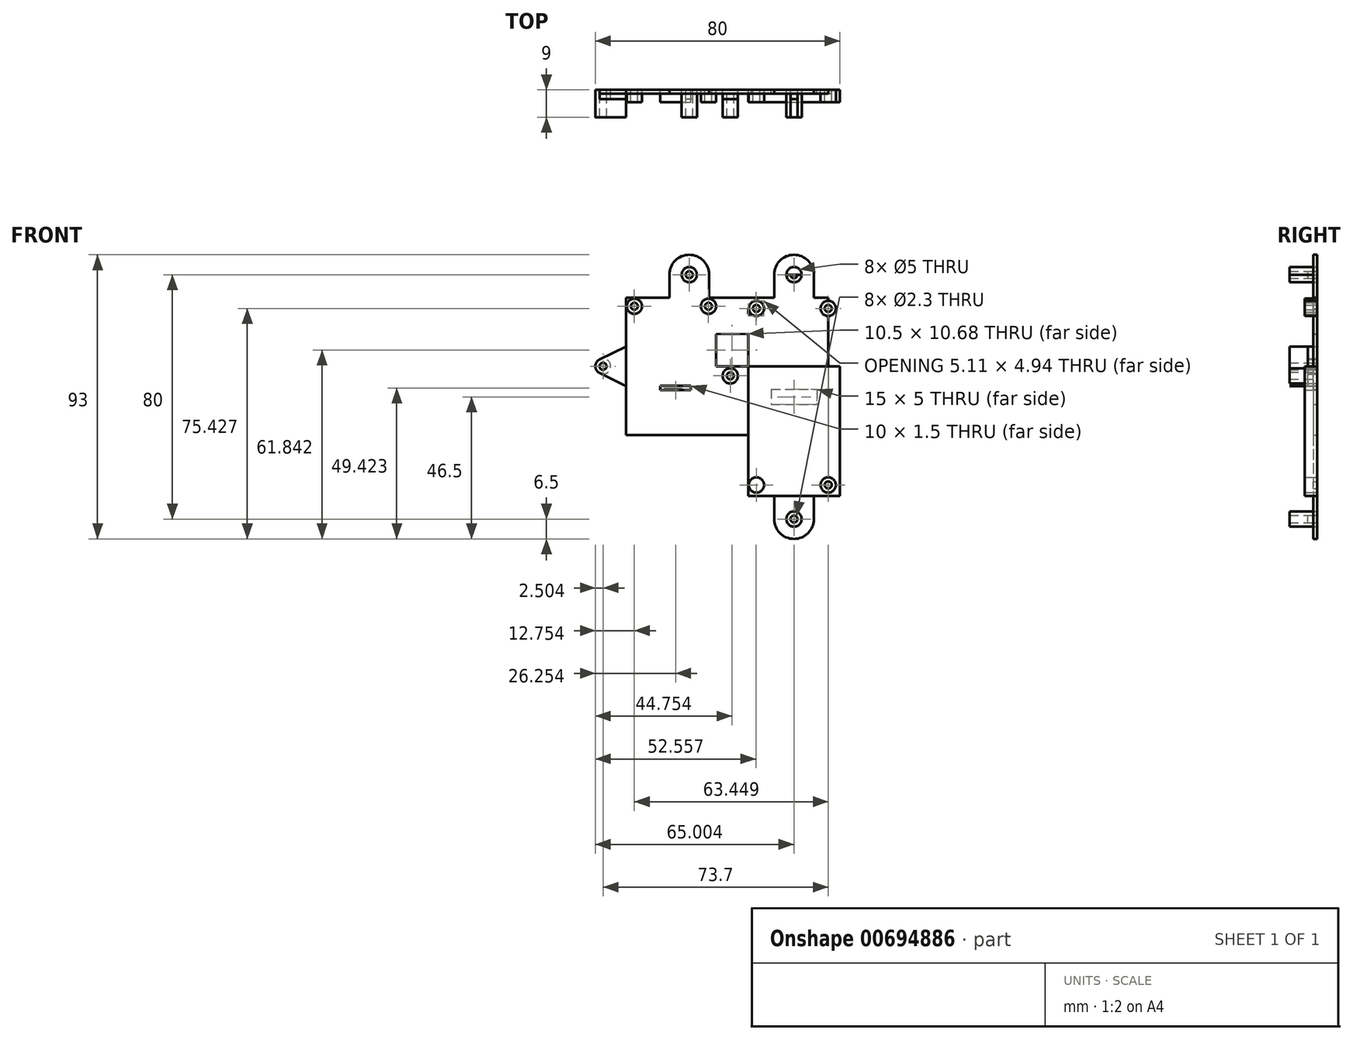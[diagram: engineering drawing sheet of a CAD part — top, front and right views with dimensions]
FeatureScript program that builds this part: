
annotation { "Feature Type Name" : "Feature", "Feature Type Description" : "" }
export const myFeature = defineFeature(function(context is Context, id is Id, definition is map)
    precondition{}
    {
        {
            var Q0;
            Q0=qCreatedBy(makeId("Front.planeOp"),FACE);
            var sketch = newSketch(context, id + "F0", { "sketchPlane" : qUnion([Q0])});
            skLineSegment(sketch, "E0.bottom", {"start": v(-16.83, 32.5) * mm, "end": v(13.17, 32.5) * mm});
            skLineSegment(sketch, "E0.top", {"start": v(-16.83, -32.5) * mm, "end": v(13.17, -32.5) * mm});
            skLineSegment(sketch, "E0.left", {"start": v(-16.83, 32.5) * mm, "end": v(-16.83, -32.5) * mm});
            skLineSegment(sketch, "E0.right", {"start": v(13.17, 32.5) * mm, "end": v(13.17, -32.5) * mm});
            skPoint(sketch, "E0.middle", {"position": v(-1.83, 0) * mm});
            skLineSegment(sketch, "E1.bottom", {"start": v(-16.83, 32.5) * mm, "end": v(-56.83, 32.5) * mm});
            skLineSegment(sketch, "E1.top", {"start": v(-16.83, -12.5) * mm, "end": v(-56.83, -12.5) * mm});
            skLineSegment(sketch, "E1.left", {"start": v(-16.83, 32.5) * mm, "end": v(-16.83, -12.5) * mm});
            skLineSegment(sketch, "E1.right", {"start": v(-56.83, 32.5) * mm, "end": v(-56.83, -12.5) * mm});
            skCircle(sketch, "E2", {"center": v(-54.08, 29.67) * mm, "radius": 2.5 * mm});
            skPoint(sketch, "E2.centerSnap0", {"position": v(-55.33, 29.67) * mm});
            skPoint(sketch, "E2.centerSnap1", {"position": v(-54.08, 30.92) * mm});
            skLineSegment(sketch, "E3", {"start": v(-51.33, 29.67) * mm, "end": v(-29.83, 29.67) * mm});
            skCircle(sketch, "E4", {"center": v(-29.83, 29.67) * mm, "radius": 2.5 * mm});
            skLineSegment(sketch, "E5", {"start": v(-40.58, 29.67) * mm, "end": v(-40.58, 3.67) * mm});
            skLineSegment(sketch, "E6", {"start": v(-40.58, 3.67) * mm, "end": v(-35.58, 3.67) * mm});
            skLineSegment(sketch, "E7", {"start": v(-35.58, 3.67) * mm, "end": v(-45.58, 3.67) * mm});
            skLineSegment(sketch, "E8", {"start": v(-45.58, 3.67) * mm, "end": v(-45.58, 2.17) * mm});
            skLineSegment(sketch, "E9", {"start": v(-45.58, 2.17) * mm, "end": v(-35.58, 2.17) * mm});
            skLineSegment(sketch, "E10", {"start": v(-35.58, 2.17) * mm, "end": v(-35.58, 3.67) * mm});
            skCircle(sketch, "E11", {"center": v(9.37, 28.95) * mm, "radius": 2.5 * mm});
            skPoint(sketch, "E11.centerSnap0", {"position": v(9.37, 30.2) * mm});
            skPoint(sketch, "E11.centerSnap1", {"position": v(10.87, 28.95) * mm});
            skLineSegment(sketch, "E12", {"start": v(-1.83, 0) * mm, "end": v(-1.83, 32.5) * mm});
            skLineSegment(sketch, "E13", {"start": v(9.37, 28.95) * mm, "end": v(-14.13, 28.95) * mm});
            skCircle(sketch, "E14", {"center": v(-14.13, 28.95) * mm, "radius": 2.5 * mm});
            skCircle(sketch, "E15.MirrorC", {"center": v(-14.13, -28.85) * mm, "radius": 2.5 * mm});
            skCircle(sketch, "E16.MirrorC", {"center": v(9.37, -28.85) * mm, "radius": 2.5 * mm});
            skLineSegment(sketch, "E17.bottom", {"start": v(-9.33, 2.5) * mm, "end": v(5.67, 2.5) * mm});
            skLineSegment(sketch, "E17.top", {"start": v(-9.33, -2.5) * mm, "end": v(5.67, -2.5) * mm});
            skLineSegment(sketch, "E17.left", {"start": v(-9.33, 2.5) * mm, "end": v(-9.33, -2.5) * mm});
            skLineSegment(sketch, "E17.right", {"start": v(5.67, 2.5) * mm, "end": v(5.67, -2.5) * mm});
            skCircle(sketch, "E18", {"center": v(9.37, 28.95) * mm, "radius": 1.15 * mm});
            skCircle(sketch, "E19", {"center": v(-14.13, 28.95) * mm, "radius": 1.15 * mm});
            skLineSegment(sketch, "E20", {"start": v(9.37, 28.95) * mm, "end": v(9.37, -26.35) * mm});
            skCircle(sketch, "E21", {"center": v(9.37, -28.85) * mm, "radius": 1.15 * mm});
            skCircle(sketch, "E22", {"center": v(-14.13, -28.85) * mm, "radius": 1.15 * mm});
            skCircle(sketch, "E23", {"center": v(-29.83, 29.67) * mm, "radius": 1.15 * mm});
            skCircle(sketch, "E24", {"center": v(-54.08, 29.67) * mm, "radius": 1.15 * mm});
            skLineSegment(sketch, "E25", {"start": v(-15.63, 27.12) * mm, "end": v(-24.08, 27.12) * mm});
            skCircle(sketch, "E26", {"center": v(-22.69, 6.88) * mm, "radius": 1.15 * mm});
            skCircle(sketch, "E27", {"center": v(-22.69, 6.88) * mm, "radius": 2.5 * mm});
            skLineSegment(sketch, "E28", {"start": v(9.37, -28.85) * mm, "end": v(9.37, -32.5) * mm});
            skLineSegment(sketch, "E29", {"start": v(9.37, -32.5) * mm, "end": v(13.17, -32.5) * mm});
            skLineSegment(sketch, "E30", {"start": v(-14.13, -28.85) * mm, "end": v(-14.13, -32.5) * mm});
            skLineSegment(sketch, "E31", {"start": v(-14.13, -32.5) * mm, "end": v(-16.83, -32.5) * mm});
            skLineSegment(sketch, "E32", {"start": v(9.37, 28.95) * mm, "end": v(9.37, 32.5) * mm});
            skLineSegment(sketch, "E33", {"start": v(9.37, 32.5) * mm, "end": v(13.17, 32.5) * mm});
            skLineSegment(sketch, "E34", {"start": v(-14.13, 28.95) * mm, "end": v(-16.83, 28.95) * mm});
            skLineSegment(sketch, "E35", {"start": v(-14.13, 28.95) * mm, "end": v(-14.13, 32.5) * mm});
            skLineSegment(sketch, "E36", {"start": v(-56.83, 10) * mm, "end": v(-64.33, 10) * mm});
            skCircle(sketch, "E37", {"center": v(-64.33, 10) * mm, "radius": 1.15 * mm});
            skCircle(sketch, "E38", {"center": v(-64.33, 10) * mm, "radius": 2.5 * mm});
            skLineSegment(sketch, "E39", {"start": v(-36.1, 32.5) * mm, "end": v(-36.1, 40) * mm});
            skCircle(sketch, "E40", {"center": v(-36.1, 40) * mm, "radius": 6.5 * mm});
            skCircle(sketch, "E41", {"center": v(-36.1, 40) * mm, "radius": 2.5 * mm});
            skCircle(sketch, "E42", {"center": v(-36.1, 40) * mm, "radius": 1.15 * mm});
            skLineSegment(sketch, "E43", {"start": v(-1.83, 32.5) * mm, "end": v(-1.83, 40) * mm});
            skCircle(sketch, "E44", {"center": v(-1.83, 40) * mm, "radius": 6.5 * mm});
            skCircle(sketch, "E45", {"center": v(-1.83, 40) * mm, "radius": 2.5 * mm});
            skCircle(sketch, "E46", {"center": v(-1.83, 40) * mm, "radius": 1.15 * mm});
            skCircle(sketch, "E47", {"center": v(-1.83, -40) * mm, "radius": 6.5 * mm});
            skCircle(sketch, "E48", {"center": v(-1.83, -40) * mm, "radius": 2.5 * mm});
            skCircle(sketch, "E49", {"center": v(-1.83, -40) * mm, "radius": 1.15 * mm});
            skLineSegment(sketch, "E50", {"start": v(-1.83, -40) * mm, "end": v(-1.83, -32.5) * mm});
            skLineSegment(sketch, "E51", {"start": v(-1.83, -40) * mm, "end": v(-8.33, -40) * mm});
            skLineSegment(sketch, "E52", {"start": v(-8.33, -40) * mm, "end": v(4.67, -40) * mm});
            skLineSegment(sketch, "E53", {"start": v(4.67, -40) * mm, "end": v(4.67, -32.5) * mm});
            skLineSegment(sketch, "E54", {"start": v(4.67, -32.5) * mm, "end": v(-8.33, -32.5) * mm});
            skLineSegment(sketch, "E55", {"start": v(-8.33, -32.5) * mm, "end": v(-8.33, -40) * mm});
            skLineSegment(sketch, "E56", {"start": v(-1.83, 40) * mm, "end": v(-8.33, 40) * mm});
            skLineSegment(sketch, "E57", {"start": v(-8.33, 40) * mm, "end": v(4.67, 40) * mm});
            skLineSegment(sketch, "E58", {"start": v(4.67, 40) * mm, "end": v(4.67, 32.5) * mm});
            skLineSegment(sketch, "E59", {"start": v(4.67, 32.5) * mm, "end": v(-8.33, 32.5) * mm});
            skLineSegment(sketch, "E60", {"start": v(-8.33, 32.5) * mm, "end": v(-8.33, 40) * mm});
            skLineSegment(sketch, "E61", {"start": v(-36.1, 40) * mm, "end": v(-42.6, 40) * mm});
            skLineSegment(sketch, "E62", {"start": v(-42.6, 40) * mm, "end": v(-42.6, 32.5) * mm});
            skLineSegment(sketch, "E63", {"start": v(-36.1, 40) * mm, "end": v(-29.6, 40) * mm});
            skLineSegment(sketch, "E64", {"start": v(-29.6, 40) * mm, "end": v(-29.6, 32.5) * mm});
            skLineSegment(sketch, "E65", {"start": v(-28.7, 20.53) * mm, "end": v(-16.83, 20.68) * mm});
            skLineSegment(sketch, "E66", {"start": v(-51.58, 29.67) * mm, "end": v(-32.33, 29.67) * mm});
            skLineSegment(sketch, "E67", {"start": v(-54.08, 29.67) * mm, "end": v(-56.83, 29.67) * mm});
            skLineSegment(sketch, "E68", {"start": v(-29.83, 29.67) * mm, "end": v(-27.33, 29.67) * mm});
            skLineSegment(sketch, "E69", {"start": v(-27.33, 29.67) * mm, "end": v(-27.33, 5.14) * mm});
            skLineSegment(sketch, "E70", {"start": v(-64.33, 10) * mm, "end": v(13.17, 10) * mm});
            skLineSegment(sketch, "E71", {"start": v(-56.83, 16.5) * mm, "end": v(-65.44, 12.24) * mm});
            skLineSegment(sketch, "E72", {"start": v(-56.83, 3.5) * mm, "end": v(-65.44, 7.76) * mm});
            skSolve(sketch);
        }
        {
            var Q0;
            Q0=makeQuery(id+"F0.imprint","IMPRINT",FACE,{"disambiguationData":[TD([[makeQuery(id+"F0.imprint","IMPRINT",EDGE,{"derivedFrom":sQuery(id+"F0.wireOp",EDGE,"E24")}),-1.0]])]});
            var Q1;
            Q1=makeQuery(id+"F0.imprint","IMPRINT",FACE,{"disambiguationData":[TD([[makeQuery(id+"F0.imprint","IMPRINT",EDGE,{"derivedFrom":sQuery(id+"F0.wireOp",EDGE,"E4")}),1.0]])]});
            var Q2;
            Q2=makeQuery(id+"F0.imprint","IMPRINT",FACE,{"disambiguationData":[TD([[makeQuery(id+"F0.imprint","IMPRINT",EDGE,{"derivedFrom":sQuery(id+"F0.wireOp",EDGE,"E19")}),-1.0]])]});
            var Q3;
            Q3=makeQuery(id+"F0.imprint","IMPRINT",FACE,{"disambiguationData":[TD([[makeQuery(id+"F0.imprint","IMPRINT",EDGE,{"derivedFrom":sQuery(id+"F0.wireOp",EDGE,"E18")}),-1.0]])]});
            var Q4;
            Q4=makeQuery(id+"F0.imprint","IMPRINT",FACE,{"disambiguationData":[TD([[makeQuery(id+"F0.imprint","IMPRINT",EDGE,{"derivedFrom":sQuery(id+"F0.wireOp",EDGE,"E15.MirrorC")}),-1.0]])]});
            var Q5;
            Q5=makeQuery(id+"F0.imprint","IMPRINT",FACE,{"disambiguationData":[TD([[makeQuery(id+"F0.imprint","IMPRINT",EDGE,{"derivedFrom":sQuery(id+"F0.wireOp",EDGE,"E16.MirrorC")}),-1.0]])]});
            var Q6;
            {var subQ0=sQuery(id+"F0.wireOp",EDGE,"E8");Q6=makeQuery(id+"F0.imprint","IMPRINT",FACE,{"disambiguationData":[TD([[makeQuery(id+"F0.imprint","IMPRINT",EDGE,{"derivedFrom":subQ0}),1.0]])]});}
            var Q7;
            {var subQ0=sQuery(id+"F0.wireOp",EDGE,"E17.top");Q7=makeQuery(id+"F0.imprint","IMPRINT",FACE,{"disambiguationData":[TD([[makeQuery(id+"F0.imprint","IMPRINT",EDGE,{"derivedFrom":subQ0}),1.0]])]});}
            var Q8;
            {var subQ5=sQuery(id+"F0.wireOp",EDGE,"E11");var subQ6=makeQuery(id+"F0.imprint","INTERSECT",VERTEX,{"derivedFrom":[subQ5,sQuery(id+"F0.wireOp",EDGE,"E20")]});Q8=makeQuery(id+"F0.imprint","IMPRINT",FACE,{"disambiguationData":[TD([[makeQuery(id+"F0.imprint","IMPRINT",EDGE,{"disambiguationData":[TD([[subQ6,1.0]])],"derivedFrom":subQ5}),1.0]])]});}
            var Q9;
            {var subQ1=sQuery(id+"F0.wireOp",EDGE,"E13");var subQ5=sQuery(id+"F0.wireOp",EDGE,"E14");var subQ8=makeQuery(id+"F0.imprint","INTERSECT",VERTEX,{"derivedFrom":[subQ1,subQ5]});Q9=makeQuery(id+"F0.imprint","IMPRINT",FACE,{"disambiguationData":[TD([[makeQuery(id+"F0.imprint","IMPRINT",EDGE,{"disambiguationData":[TD([[subQ8,-1.0]])],"derivedFrom":subQ1}),1.0]])]});}
            extrude(context, id + "F1", {"entities" : qUnion([Q0, Q1, Q2, Q3, Q4, Q5, Q6, Q7, Q8, Q9]), "depth" : 4 * mm, "offsetDistance" : 25 * mm});
        }
        {
            var Q0;
            {var subQ1=sQuery(id+"F0.wireOp",EDGE,"E11");var subQ13=sQuery(id+"F0.wireOp",EDGE,"E20");var subQ15=makeQuery(id+"F0.imprint","INTERSECT",VERTEX,{"derivedFrom":[subQ1,subQ13]});Q0=makeQuery(id+"F0.imprint","IMPRINT",FACE,{"disambiguationData":[TD([[makeQuery(id+"F0.imprint","IMPRINT",EDGE,{"disambiguationData":[TD([[subQ15,1.0]])],"derivedFrom":subQ1}),-1.0]])]});}
            var Q1;
            {var subQ1=sQuery(id+"F0.wireOp",EDGE,"E1.left");var subQ16=makeQuery(id+"F0.imprint","IMPRINT",VERTEX,{"disambiguationData":[OD(0.0)],"derivedFrom":subQ1});Q1=makeQuery(id+"F0.imprint","IMPRINT",FACE,{"disambiguationData":[TD([[makeQuery(id+"F0.imprint","IMPRINT",EDGE,{"disambiguationData":[TD([[subQ16,-1.0]])],"derivedFrom":subQ1}),1.0]])]});}
            var Q2;
            {var subQ0=sQuery(id+"F0.wireOp",EDGE,"E12");var subQ5=sQuery(id+"F0.wireOp",EDGE,"E13");var subQ6=makeQuery(id+"F0.imprint","INTERSECT",VERTEX,{"derivedFrom":[subQ0,subQ5]});Q2=makeQuery(id+"F0.imprint","IMPRINT",FACE,{"disambiguationData":[TD([[makeQuery(id+"F0.imprint","IMPRINT",EDGE,{"disambiguationData":[TD([[subQ6,1.0]])],"derivedFrom":subQ5}),-1.0]])]});}
            var Q3;
            {var subQ0=sQuery(id+"F0.wireOp",EDGE,"E12");var subQ5=sQuery(id+"F0.wireOp",EDGE,"E13");var subQ6=makeQuery(id+"F0.imprint","INTERSECT",VERTEX,{"derivedFrom":[subQ0,subQ5]});Q3=makeQuery(id+"F0.imprint","IMPRINT",FACE,{"disambiguationData":[TD([[makeQuery(id+"F0.imprint","IMPRINT",EDGE,{"disambiguationData":[TD([[subQ6,-1.0]])],"derivedFrom":subQ5}),-1.0]])]});}
            var Q4;
            {var subQ0=sQuery(id+"F0.wireOp",EDGE,"E35");var subQ1=sQuery(id+"F0.wireOp",EDGE,"E0.bottom");var subQ2=makeQuery(id+"F0.imprint","INTERSECT",VERTEX,{"derivedFrom":[subQ1,subQ0]});Q4=makeQuery(id+"F0.imprint","IMPRINT",FACE,{"disambiguationData":[TD([[makeQuery(id+"F0.imprint","IMPRINT",EDGE,{"disambiguationData":[TD([[subQ2,-1.0]])],"derivedFrom":subQ1}),-1.0]])]});}
            var Q5;
            {var subQ9=sQuery(id+"F0.wireOp",EDGE,"E33");Q5=makeQuery(id+"F0.imprint","IMPRINT",FACE,{"disambiguationData":[TD([[makeQuery(id+"F0.imprint","IMPRINT",EDGE,{"derivedFrom":subQ9}),-1.0]])]});}
            var Q6;
            {var subQ3=sQuery(id+"F0.wireOp",EDGE,"E11");var subQ7=sQuery(id+"F0.wireOp",EDGE,"E13");var subQ9=makeQuery(id+"F0.imprint","INTERSECT",VERTEX,{"derivedFrom":[subQ3,subQ7]});Q6=makeQuery(id+"F0.imprint","IMPRINT",FACE,{"disambiguationData":[TD([[makeQuery(id+"F0.imprint","IMPRINT",EDGE,{"disambiguationData":[TD([[subQ9,1.0]])],"derivedFrom":subQ3}),-1.0]])]});}
            var Q7;
            {var subQ0=sQuery(id+"F0.wireOp",EDGE,"E44");var subQ1=sQuery(id+"F0.wireOp",EDGE,"E12");var subQ2=makeQuery(id+"F0.imprint","INTERSECT",VERTEX,{"derivedFrom":[subQ1,subQ0]});Q7=makeQuery(id+"F0.imprint","IMPRINT",FACE,{"disambiguationData":[TD([[makeQuery(id+"F0.imprint","IMPRINT",EDGE,{"disambiguationData":[TD([[subQ2,-1.0]])],"derivedFrom":subQ1}),-1.0]])]});}
            var Q8;
            {var subQ0=sQuery(id+"F0.wireOp",EDGE,"E45");Q8=makeQuery(id+"F0.imprint","IMPRINT",FACE,{"disambiguationData":[TD([[makeQuery(id+"F0.imprint","IMPRINT",EDGE,{"derivedFrom":subQ0}),-1.0]])]});}
            var Q9;
            {var subQ0=sQuery(id+"F0.wireOp",EDGE,"E44");var subQ1=sQuery(id+"F0.wireOp",EDGE,"E12");var subQ2=makeQuery(id+"F0.imprint","INTERSECT",VERTEX,{"derivedFrom":[subQ1,subQ0]});Q9=makeQuery(id+"F0.imprint","IMPRINT",FACE,{"disambiguationData":[TD([[makeQuery(id+"F0.imprint","IMPRINT",EDGE,{"disambiguationData":[TD([[subQ2,-1.0]])],"derivedFrom":subQ1}),1.0]])]});}
            var Q10;
            Q10=makeQuery(id+"F0.imprint","IMPRINT",FACE,{"disambiguationData":[TD([[makeQuery(id+"F0.imprint","IMPRINT",EDGE,{"derivedFrom":sQuery(id+"F0.wireOp",EDGE,"E15.MirrorC")}),1.0]])]});
            var Q11;
            {var subQ7=sQuery(id+"F0.wireOp",EDGE,"E29");Q11=makeQuery(id+"F0.imprint","IMPRINT",FACE,{"disambiguationData":[TD([[makeQuery(id+"F0.imprint","IMPRINT",EDGE,{"derivedFrom":subQ7}),1.0]])]});}
            var Q12;
            {var subQ0=sQuery(id+"F0.wireOp",EDGE,"E47");var subQ1=sQuery(id+"F0.wireOp",EDGE,"E0.top");var subQ2=makeQuery(id+"F0.imprint","INTERSECT",VERTEX,{"disambiguationData":[OD(0.0)],"derivedFrom":[subQ1,subQ0]});Q12=makeQuery(id+"F0.imprint","IMPRINT",FACE,{"disambiguationData":[TD([[makeQuery(id+"F0.imprint","IMPRINT",EDGE,{"disambiguationData":[TD([[subQ2,-1.0]])],"derivedFrom":subQ1}),1.0]])]});}
            var Q13;
            {var subQ3=sQuery(id+"F0.wireOp",EDGE,"E48");Q13=makeQuery(id+"F0.imprint","IMPRINT",FACE,{"disambiguationData":[TD([[makeQuery(id+"F0.imprint","IMPRINT",EDGE,{"derivedFrom":subQ3}),-1.0]])]});}
            var Q14;
            {var subQ1=sQuery(id+"F0.wireOp",EDGE,"E1.top");var subQ4=sQuery(id+"F0.wireOp",EDGE,"H2bswWBa-21Oe-qWVp-0FWu-aY4BrK7KTLVz");var subQ5=makeQuery(id+"F0.imprint","INTERSECT",VERTEX,{"derivedFrom":[subQ1,subQ4]});Q14=makeQuery(id+"F0.imprint","IMPRINT",FACE,{"disambiguationData":[TD([[makeQuery(id+"F0.imprint","IMPRINT",EDGE,{"disambiguationData":[TD([[subQ5,1.0]])],"derivedFrom":subQ1}),-1.0]])]});}
            var Q15;
            {var subQ1=sQuery(id+"F0.wireOp",EDGE,"E0.left");var subQ4=sQuery(id+"F0.wireOp",EDGE,"H2bswWBa-21Oe-qWVp-0FWu-aY4BrK7KTLVz");var subQ5=makeQuery(id+"F0.imprint","INTERSECT",VERTEX,{"derivedFrom":[subQ1,subQ4]});Q15=makeQuery(id+"F0.imprint","IMPRINT",FACE,{"disambiguationData":[TD([[makeQuery(id+"F0.imprint","IMPRINT",EDGE,{"disambiguationData":[TD([[subQ5,1.0]])],"derivedFrom":subQ1}),1.0]])]});}
            var Q16;
            {var subQ0=sQuery(id+"F0.wireOp",EDGE,"H2bswWBa-21Oe-qWVp-0FWu-aY4BrK7KTLVz");var subQ1=sQuery(id+"F0.wireOp",EDGE,"E0.left");var subQ2=makeQuery(id+"F0.imprint","INTERSECT",VERTEX,{"derivedFrom":[subQ1,subQ0]});Q16=makeQuery(id+"F0.imprint","IMPRINT",FACE,{"disambiguationData":[TD([[makeQuery(id+"F0.imprint","IMPRINT",EDGE,{"disambiguationData":[TD([[subQ2,1.0]])],"derivedFrom":subQ1}),-1.0]])]});}
            var Q17;
            Q17=makeQuery(id+"F0.imprint","IMPRINT",FACE,{"disambiguationData":[TD([[makeQuery(id+"F0.imprint","IMPRINT",EDGE,{"derivedFrom":sQuery(id+"F0.wireOp",EDGE,"E2")}),-1.0]])]});
            var Q18;
            {var subQ0=sQuery(id+"F0.wireOp",EDGE,"E5");var subQ1=sQuery(id+"F0.wireOp",EDGE,"E3");var subQ2=makeQuery(id+"F0.imprint","INTERSECT",VERTEX,{"derivedFrom":[subQ1,subQ0]});Q18=makeQuery(id+"F0.imprint","IMPRINT",FACE,{"disambiguationData":[TD([[makeQuery(id+"F0.imprint","IMPRINT",EDGE,{"disambiguationData":[TD([[subQ2,1.0]])],"derivedFrom":subQ1}),-1.0]])]});}
            var Q19;
            {var subQ0=sQuery(id+"F0.wireOp",EDGE,"E5");var subQ1=sQuery(id+"F0.wireOp",EDGE,"E3");var subQ2=makeQuery(id+"F0.imprint","INTERSECT",VERTEX,{"derivedFrom":[subQ1,subQ0]});Q19=makeQuery(id+"F0.imprint","IMPRINT",FACE,{"disambiguationData":[TD([[makeQuery(id+"F0.imprint","IMPRINT",EDGE,{"disambiguationData":[TD([[subQ2,-1.0]])],"derivedFrom":subQ1}),-1.0]])]});}
            var Q20;
            {var subQ5=sQuery(id+"F0.wireOp",EDGE,"E1.bottom");var subQ6=makeQuery(id+"F0.imprint","INTERSECT",VERTEX,{"derivedFrom":[subQ5,sQuery(id+"F0.wireOp",EDGE,"E41")]});Q20=makeQuery(id+"F0.imprint","IMPRINT",FACE,{"disambiguationData":[TD([[makeQuery(id+"F0.imprint","IMPRINT",EDGE,{"disambiguationData":[TD([[subQ6,1.0]])],"derivedFrom":subQ5}),1.0]])]});}
            var Q21;
            {var subQ0=sQuery(id+"F0.wireOp",EDGE,"E41");Q21=makeQuery(id+"F0.imprint","IMPRINT",FACE,{"disambiguationData":[TD([[makeQuery(id+"F0.imprint","IMPRINT",EDGE,{"derivedFrom":subQ0}),-1.0]])]});}
            var Q22;
            {var subQ0=sQuery(id+"F0.wireOp",EDGE,"E1.right");var subQ1=makeQuery(id+"F0.imprint","INTERSECT",VERTEX,{"derivedFrom":[subQ0,sQuery(id+"F0.wireOp",EDGE,"E38")]});Q22=makeQuery(id+"F0.imprint","IMPRINT",FACE,{"disambiguationData":[TD([[makeQuery(id+"F0.imprint","IMPRINT",EDGE,{"disambiguationData":[TD([[subQ1,1.0]])],"derivedFrom":subQ0}),1.0]])]});}
            var Q23;
            {var subQ0=sQuery(id+"F0.wireOp",EDGE,"E38");Q23=makeQuery(id+"F0.imprint","IMPRINT",FACE,{"disambiguationData":[TD([[makeQuery(id+"F0.imprint","IMPRINT",EDGE,{"derivedFrom":subQ0}),-1.0]])]});}
            var Q24;
            {var subQ0=sQuery(id+"F0.wireOp",EDGE,"E32");var subQ1=sQuery(id+"F0.wireOp",EDGE,"E13");var subQ2=makeQuery(id+"F0.imprint","INTERSECT",VERTEX,{"derivedFrom":[subQ1,subQ0]});Q24=makeQuery(id+"F0.imprint","IMPRINT",FACE,{"disambiguationData":[TD([[makeQuery(id+"F0.imprint","IMPRINT",EDGE,{"disambiguationData":[TD([[subQ2,-1.0]])],"derivedFrom":subQ1}),1.0]])]});}
            var Q25;
            {var subQ0=sQuery(id+"F0.wireOp",EDGE,"E32");var subQ1=sQuery(id+"F0.wireOp",EDGE,"E13");var subQ2=makeQuery(id+"F0.imprint","INTERSECT",VERTEX,{"derivedFrom":[subQ1,subQ0]});Q25=makeQuery(id+"F0.imprint","IMPRINT",FACE,{"disambiguationData":[TD([[makeQuery(id+"F0.imprint","IMPRINT",EDGE,{"disambiguationData":[TD([[subQ2,-1.0]])],"derivedFrom":subQ1}),-1.0]])]});}
            var Q26;
            {var subQ1=sQuery(id+"F0.wireOp",EDGE,"E13");var subQ3=sQuery(id+"F0.wireOp",EDGE,"E19");var subQ4=makeQuery(id+"F0.imprint","INTERSECT",VERTEX,{"derivedFrom":[subQ1,subQ3]});Q26=makeQuery(id+"F0.imprint","IMPRINT",FACE,{"disambiguationData":[TD([[makeQuery(id+"F0.imprint","IMPRINT",EDGE,{"disambiguationData":[TD([[subQ4,1.0]])],"derivedFrom":subQ3}),1.0]])]});}
            var Q27;
            {var subQ0=sQuery(id+"F0.wireOp",EDGE,"E35");var subQ1=sQuery(id+"F0.wireOp",EDGE,"E19");var subQ2=makeQuery(id+"F0.imprint","INTERSECT",VERTEX,{"derivedFrom":[subQ1,subQ0]});Q27=makeQuery(id+"F0.imprint","IMPRINT",FACE,{"disambiguationData":[TD([[makeQuery(id+"F0.imprint","IMPRINT",EDGE,{"disambiguationData":[TD([[subQ2,-1.0]])],"derivedFrom":subQ1}),1.0]])]});}
            var Q28;
            {var subQ1=sQuery(id+"F0.wireOp",EDGE,"E13");var subQ3=sQuery(id+"F0.wireOp",EDGE,"E19");var subQ4=makeQuery(id+"F0.imprint","INTERSECT",VERTEX,{"derivedFrom":[subQ1,subQ3]});Q28=makeQuery(id+"F0.imprint","IMPRINT",FACE,{"disambiguationData":[TD([[makeQuery(id+"F0.imprint","IMPRINT",EDGE,{"disambiguationData":[TD([[subQ4,-1.0]])],"derivedFrom":subQ3}),1.0]])]});}
            var Q29;
            Q29=makeQuery(id+"F0.imprint","IMPRINT",FACE,{"disambiguationData":[TD([[makeQuery(id+"F0.imprint","IMPRINT",EDGE,{"derivedFrom":sQuery(id+"F0.wireOp",EDGE,"E23")}),1.0]])]});
            var Q30;
            Q30=makeQuery(id+"F0.imprint","IMPRINT",FACE,{"disambiguationData":[TD([[makeQuery(id+"F0.imprint","IMPRINT",EDGE,{"derivedFrom":sQuery(id+"F0.wireOp",EDGE,"E24")}),1.0]])]});
            var Q31;
            Q31=makeQuery(id+"F0.imprint","IMPRINT",FACE,{"disambiguationData":[TD([[makeQuery(id+"F0.imprint","IMPRINT",EDGE,{"derivedFrom":sQuery(id+"F0.wireOp",EDGE,"E21")}),1.0]])]});
            var Q32;
            Q32=makeQuery(id+"F0.imprint","IMPRINT",FACE,{"disambiguationData":[TD([[makeQuery(id+"F0.imprint","IMPRINT",EDGE,{"derivedFrom":sQuery(id+"F0.wireOp",EDGE,"E22")}),1.0]])]});
            var Q33;
            {var subQ1=sQuery(id+"F0.wireOp",EDGE,"E0.left");var subQ3=sQuery(id+"F0.wireOp",EDGE,"vLtY0Nj5-JtJk-fO2F-L4fz-pWqKutG9Hdl8");var subQ4=makeQuery(id+"F0.imprint","INTERSECT",VERTEX,{"derivedFrom":[subQ1,subQ3]});Q33=makeQuery(id+"F0.imprint","IMPRINT",FACE,{"disambiguationData":[TD([[makeQuery(id+"F0.imprint","IMPRINT",EDGE,{"disambiguationData":[TD([[subQ4,-1.0]])],"derivedFrom":subQ3}),-1.0]])]});}
            var Q34;
            {var subQ3=sQuery(id+"F0.wireOp",EDGE,"s8Qitc2e-HOJI-ncwY-YY4z-nysmE6fKBLHD");Q34=makeQuery(id+"F0.imprint","IMPRINT",FACE,{"disambiguationData":[TD([[makeQuery(id+"F0.imprint","IMPRINT",EDGE,{"derivedFrom":subQ3}),1.0]])]});}
            var Q35;
            {var subQ3=sQuery(id+"F0.wireOp",EDGE,"rnlotXtN-yekX-c3Ef-nKGb-O9DUJwXdL25D");Q35=makeQuery(id+"F0.imprint","IMPRINT",FACE,{"disambiguationData":[TD([[makeQuery(id+"F0.imprint","IMPRINT",EDGE,{"derivedFrom":subQ3}),-1.0]])]});}
            var Q36;
            {var subQ3=sQuery(id+"F0.wireOp",EDGE,"E62");Q36=makeQuery(id+"F0.imprint","IMPRINT",FACE,{"disambiguationData":[TD([[makeQuery(id+"F0.imprint","IMPRINT",EDGE,{"derivedFrom":subQ3}),1.0]])]});}
            var Q37;
            {var subQ3=sQuery(id+"F0.wireOp",EDGE,"E64");Q37=makeQuery(id+"F0.imprint","IMPRINT",FACE,{"disambiguationData":[TD([[makeQuery(id+"F0.imprint","IMPRINT",EDGE,{"derivedFrom":subQ3}),-1.0]])]});}
            var Q38;
            {var subQ5=sQuery(id+"F0.wireOp",EDGE,"E60");Q38=makeQuery(id+"F0.imprint","IMPRINT",FACE,{"disambiguationData":[TD([[makeQuery(id+"F0.imprint","IMPRINT",EDGE,{"derivedFrom":subQ5}),-1.0]])]});}
            var Q39;
            {var subQ5=sQuery(id+"F0.wireOp",EDGE,"E58");Q39=makeQuery(id+"F0.imprint","IMPRINT",FACE,{"disambiguationData":[TD([[makeQuery(id+"F0.imprint","IMPRINT",EDGE,{"derivedFrom":subQ5}),-1.0]])]});}
            var Q40;
            {var subQ0=sQuery(id+"F0.wireOp",EDGE,"wpgFawej-uTnE-nY6H-FU0d-e7JS0PavbXeQ");var subQ1=sQuery(id+"F0.wireOp",EDGE,"9S27bfH2-aeVg-8c6K-cwQt-1v0k5dwx2PAc");var subQ2=makeQuery(id+"F0.imprint","INTERSECT",VERTEX,{"derivedFrom":[subQ1,subQ0]});Q40=makeQuery(id+"F0.imprint","IMPRINT",FACE,{"disambiguationData":[TD([[makeQuery(id+"F0.imprint","IMPRINT",EDGE,{"disambiguationData":[TD([[subQ2,-1.0]])],"derivedFrom":subQ1}),-1.0]])]});}
            var Q41;
            {var subQ0=sQuery(id+"F0.wireOp",EDGE,"wpgFawej-uTnE-nY6H-FU0d-e7JS0PavbXeQ");var subQ1=sQuery(id+"F0.wireOp",EDGE,"9S27bfH2-aeVg-8c6K-cwQt-1v0k5dwx2PAc");var subQ2=makeQuery(id+"F0.imprint","INTERSECT",VERTEX,{"derivedFrom":[subQ1,subQ0]});Q41=makeQuery(id+"F0.imprint","IMPRINT",FACE,{"disambiguationData":[TD([[makeQuery(id+"F0.imprint","IMPRINT",EDGE,{"disambiguationData":[TD([[subQ2,-1.0]])],"derivedFrom":subQ1}),1.0]])]});}
            var Q42;
            {var subQ0=sQuery(id+"F0.wireOp",EDGE,"WzKnqnnp-cW6H-dtaq-a9nc-BIZvJngSIy6v");var subQ5=sQuery(id+"F0.wireOp",EDGE,"wpgFawej-uTnE-nY6H-FU0d-e7JS0PavbXeQ");var subQ6=makeQuery(id+"F0.imprint","INTERSECT",VERTEX,{"derivedFrom":[subQ5,subQ0]});Q42=makeQuery(id+"F0.imprint","IMPRINT",FACE,{"disambiguationData":[TD([[makeQuery(id+"F0.imprint","IMPRINT",EDGE,{"disambiguationData":[TD([[subQ6,-1.0]])],"derivedFrom":subQ5}),-1.0]])]});}
            var Q43;
            {var subQ0=sQuery(id+"F0.wireOp",EDGE,"TDiUslce-FG7m-lDCQ-hQCu-48WjQpyJGrM8");var subQ1=sQuery(id+"F0.wireOp",EDGE,"Gpz7nxuA-fGOU-zDca-uDqp-oelFocvOXtPt");var subQ2=makeQuery(id+"F0.imprint","INTERSECT",VERTEX,{"derivedFrom":[subQ1,subQ0]});Q43=makeQuery(id+"F0.imprint","IMPRINT",FACE,{"disambiguationData":[TD([[makeQuery(id+"F0.imprint","IMPRINT",EDGE,{"disambiguationData":[TD([[subQ2,-1.0]])],"derivedFrom":subQ1}),-1.0]])]});}
            var Q44;
            {var subQ1=sQuery(id+"F0.wireOp",EDGE,"E1.top");var subQ3=sQuery(id+"F0.wireOp",EDGE,"9S27bfH2-aeVg-8c6K-cwQt-1v0k5dwx2PAc");var subQ4=makeQuery(id+"F0.imprint","INTERSECT",VERTEX,{"derivedFrom":[subQ1,subQ3]});Q44=makeQuery(id+"F0.imprint","IMPRINT",FACE,{"disambiguationData":[TD([[makeQuery(id+"F0.imprint","IMPRINT",EDGE,{"disambiguationData":[TD([[subQ4,1.0]])],"derivedFrom":subQ3}),-1.0]])]});}
            var Q45;
            {var subQ3=sQuery(id+"F0.wireOp",EDGE,"U70AJvk3-q6Ap-TPiJ-vSA6-dHJ4n5ZZM8l7");Q45=makeQuery(id+"F0.imprint","IMPRINT",FACE,{"disambiguationData":[TD([[makeQuery(id+"F0.imprint","IMPRINT",EDGE,{"derivedFrom":subQ3}),-1.0]])]});}
            var Q46;
            {var subQ0=sQuery(id+"F0.wireOp",EDGE,"TDiUslce-FG7m-lDCQ-hQCu-48WjQpyJGrM8");var subQ1=sQuery(id+"F0.wireOp",EDGE,"Gpz7nxuA-fGOU-zDca-uDqp-oelFocvOXtPt");var subQ2=makeQuery(id+"F0.imprint","INTERSECT",VERTEX,{"derivedFrom":[subQ1,subQ0]});Q46=makeQuery(id+"F0.imprint","IMPRINT",FACE,{"disambiguationData":[TD([[makeQuery(id+"F0.imprint","IMPRINT",EDGE,{"disambiguationData":[TD([[subQ2,-1.0]])],"derivedFrom":subQ1}),1.0]])]});}
            var Q47;
            {var subQ0=sQuery(id+"F0.wireOp",EDGE,"E55");Q47=makeQuery(id+"F0.imprint","IMPRINT",FACE,{"disambiguationData":[TD([[makeQuery(id+"F0.imprint","IMPRINT",EDGE,{"derivedFrom":subQ0}),1.0]])]});}
            var Q48;
            {var subQ0=sQuery(id+"F0.wireOp",EDGE,"E53");Q48=makeQuery(id+"F0.imprint","IMPRINT",FACE,{"disambiguationData":[TD([[makeQuery(id+"F0.imprint","IMPRINT",EDGE,{"derivedFrom":subQ0}),1.0]])]});}
            var Q49;
            {var subQ3=sQuery(id+"F0.wireOp",EDGE,"E14");var subQ5=sQuery(id+"F0.wireOp",EDGE,"E35");var subQ6=makeQuery(id+"F0.imprint","INTERSECT",VERTEX,{"derivedFrom":[subQ3,subQ5]});Q49=makeQuery(id+"F0.imprint","IMPRINT",FACE,{"disambiguationData":[TD([[makeQuery(id+"F0.imprint","IMPRINT",EDGE,{"disambiguationData":[TD([[subQ6,-1.0]])],"derivedFrom":subQ3}),-1.0]])]});}
            var Q50;
            {var subQ9=sQuery(id+"F0.wireOp",EDGE,"LjoRHYEq-4y9t-VGf0-s3ML-qFKd4Cbp655V");var subQ10=sQuery(id+"F0.wireOp",EDGE,"E1.left");var subQ11=makeQuery(id+"F0.imprint","INTERSECT",VERTEX,{"derivedFrom":[subQ10,subQ9]});Q50=makeQuery(id+"F0.imprint","IMPRINT",FACE,{"disambiguationData":[TD([[makeQuery(id+"F0.imprint","IMPRINT",EDGE,{"disambiguationData":[TD([[subQ11,1.0]])],"derivedFrom":subQ10}),1.0]])]});}
            var Q51;
            {var subQ0=sQuery(id+"F0.wireOp",EDGE,"E34");var subQ1=sQuery(id+"F0.wireOp",EDGE,"E1.left");var subQ2=makeQuery(id+"F0.imprint","INTERSECT",VERTEX,{"derivedFrom":[subQ1,subQ0]});Q51=makeQuery(id+"F0.imprint","IMPRINT",FACE,{"disambiguationData":[TD([[makeQuery(id+"F0.imprint","IMPRINT",EDGE,{"disambiguationData":[TD([[subQ2,-1.0]])],"derivedFrom":subQ1}),1.0]])]});}
            var Q52;
            {var subQ0=sQuery(id+"F0.wireOp",EDGE,"E32");var subQ1=sQuery(id+"F0.wireOp",EDGE,"E18");var subQ2=makeQuery(id+"F0.imprint","INTERSECT",VERTEX,{"derivedFrom":[subQ1,subQ0]});Q52=makeQuery(id+"F0.imprint","IMPRINT",FACE,{"disambiguationData":[TD([[makeQuery(id+"F0.imprint","IMPRINT",EDGE,{"disambiguationData":[TD([[subQ2,1.0]])],"derivedFrom":subQ1}),1.0]])]});}
            var Q53;
            {var subQ0=sQuery(id+"F0.wireOp",EDGE,"E66");var subQ3=sQuery(id+"F0.wireOp",EDGE,"E5");var subQ4=makeQuery(id+"F0.imprint","INTERSECT",VERTEX,{"derivedFrom":[subQ3,subQ0]});Q53=makeQuery(id+"F0.imprint","IMPRINT",FACE,{"disambiguationData":[TD([[makeQuery(id+"F0.imprint","IMPRINT",EDGE,{"disambiguationData":[TD([[subQ4,-1.0]])],"derivedFrom":subQ3}),1.0]])]});}
            var Q54;
            {var subQ0=sQuery(id+"F0.wireOp",EDGE,"E65");var subQ1=sQuery(id+"F0.wireOp",EDGE,"E1.left");var subQ2=makeQuery(id+"F0.imprint","INTERSECT",VERTEX,{"derivedFrom":[subQ1,subQ0]});Q54=makeQuery(id+"F0.imprint","IMPRINT",FACE,{"disambiguationData":[TD([[makeQuery(id+"F0.imprint","IMPRINT",EDGE,{"disambiguationData":[TD([[subQ2,-1.0]])],"derivedFrom":subQ1}),-1.0]])]});}
            extrude(context, id + "F2", {"entities" : qUnion([Q0, Q1, Q2, Q3, Q4, Q5, Q6, Q7, Q8, Q9, Q10, Q11, Q12, Q13, Q14, Q15, Q16, Q17, Q18, Q19, Q20, Q21, Q22, Q23, Q24, Q25, Q26, Q27, Q28, Q29, Q30, Q31, Q32, Q33, Q34, Q35, Q36, Q37, Q38, Q39, Q40, Q41, Q42, Q43, Q44, Q45, Q46, Q47, Q48, Q49, Q50, Q51, Q52, Q53, Q54]), "depth" : 1.2 * mm, "offsetDistance" : 25 * mm});
        }
        {
            var Q0;
            {var subQ0=sQuery(id+"F0.wireOp",EDGE,"z3bIMlkc-Sqp3-YFfb-OgYx-sXrnVvqoU3hI");var subQ1=sQuery(id+"F0.wireOp",EDGE,"E37");var subQ2=makeQuery(id+"F0.imprint","INTERSECT",VERTEX,{"disambiguationData":[OD(0.0)],"derivedFrom":[subQ1,subQ0]});Q0=makeQuery(id+"F0.imprint","IMPRINT",FACE,{"disambiguationData":[TD([[makeQuery(id+"F0.imprint","IMPRINT",EDGE,{"disambiguationData":[TD([[subQ2,-1.0]])],"derivedFrom":subQ1}),-1.0]])]});}
            var Q1;
            {var subQ0=sQuery(id+"F0.wireOp",EDGE,"E38");var subQ1=sQuery(id+"F0.wireOp",EDGE,"E36");var subQ2=makeQuery(id+"F0.imprint","INTERSECT",VERTEX,{"derivedFrom":[subQ1,subQ0]});Q1=makeQuery(id+"F0.imprint","IMPRINT",FACE,{"disambiguationData":[TD([[makeQuery(id+"F0.imprint","IMPRINT",EDGE,{"disambiguationData":[TD([[subQ2,-1.0]])],"derivedFrom":subQ1}),-1.0]])]});}
            var Q2;
            {var subQ0=sQuery(id+"F0.wireOp",EDGE,"E38");var subQ1=sQuery(id+"F0.wireOp",EDGE,"E36");var subQ2=makeQuery(id+"F0.imprint","INTERSECT",VERTEX,{"derivedFrom":[subQ1,subQ0]});Q2=makeQuery(id+"F0.imprint","IMPRINT",FACE,{"disambiguationData":[TD([[makeQuery(id+"F0.imprint","IMPRINT",EDGE,{"disambiguationData":[TD([[subQ2,-1.0]])],"derivedFrom":subQ1}),1.0]])]});}
            var Q3;
            Q3=makeQuery(id+"F0.imprint","IMPRINT",FACE,{"disambiguationData":[TD([[makeQuery(id+"F0.imprint","IMPRINT",EDGE,{"derivedFrom":sQuery(id+"F0.wireOp",EDGE,"E26")}),-1.0]])]});
            var Q4;
            {var subQ0=sQuery(id+"F0.wireOp",EDGE,"wpgFawej-uTnE-nY6H-FU0d-e7JS0PavbXeQ");var subQ1=sQuery(id+"F0.wireOp",EDGE,"Gpz7nxuA-fGOU-zDca-uDqp-oelFocvOXtPt");var subQ2=makeQuery(id+"F0.imprint","INTERSECT",VERTEX,{"derivedFrom":[subQ1,subQ0]});Q4=makeQuery(id+"F0.imprint","IMPRINT",FACE,{"disambiguationData":[TD([[makeQuery(id+"F0.imprint","IMPRINT",EDGE,{"disambiguationData":[TD([[subQ2,-1.0]])],"derivedFrom":subQ1}),-1.0]])]});}
            var Q5;
            {var subQ0=sQuery(id+"F0.wireOp",EDGE,"Suqf36BG-M7e0-ZgLu-wpgL-xeVtndynmz1x");var subQ1=sQuery(id+"F0.wireOp",EDGE,"9S27bfH2-aeVg-8c6K-cwQt-1v0k5dwx2PAc");var subQ2=makeQuery(id+"F0.imprint","INTERSECT",VERTEX,{"derivedFrom":[subQ1,subQ0]});Q5=makeQuery(id+"F0.imprint","IMPRINT",FACE,{"disambiguationData":[TD([[makeQuery(id+"F0.imprint","IMPRINT",EDGE,{"disambiguationData":[TD([[subQ2,-1.0]])],"derivedFrom":subQ1}),-1.0]])]});}
            var Q6;
            {var subQ0=sQuery(id+"F0.wireOp",EDGE,"Suqf36BG-M7e0-ZgLu-wpgL-xeVtndynmz1x");var subQ1=sQuery(id+"F0.wireOp",EDGE,"9S27bfH2-aeVg-8c6K-cwQt-1v0k5dwx2PAc");var subQ2=makeQuery(id+"F0.imprint","INTERSECT",VERTEX,{"derivedFrom":[subQ1,subQ0]});Q6=makeQuery(id+"F0.imprint","IMPRINT",FACE,{"disambiguationData":[TD([[makeQuery(id+"F0.imprint","IMPRINT",EDGE,{"disambiguationData":[TD([[subQ2,-1.0]])],"derivedFrom":subQ1}),1.0]])]});}
            var Q7;
            {var subQ0=sQuery(id+"F0.wireOp",EDGE,"WzKnqnnp-cW6H-dtaq-a9nc-BIZvJngSIy6v");var subQ1=sQuery(id+"F0.wireOp",EDGE,"wpgFawej-uTnE-nY6H-FU0d-e7JS0PavbXeQ");var subQ2=makeQuery(id+"F0.imprint","INTERSECT",VERTEX,{"derivedFrom":[subQ1,subQ0]});Q7=makeQuery(id+"F0.imprint","IMPRINT",FACE,{"disambiguationData":[TD([[makeQuery(id+"F0.imprint","IMPRINT",EDGE,{"disambiguationData":[TD([[subQ2,-1.0]])],"derivedFrom":subQ1}),1.0]])]});}
            var Q8;
            {var subQ0=sQuery(id+"F0.wireOp",EDGE,"wpgFawej-uTnE-nY6H-FU0d-e7JS0PavbXeQ");var subQ1=sQuery(id+"F0.wireOp",EDGE,"Gpz7nxuA-fGOU-zDca-uDqp-oelFocvOXtPt");var subQ2=makeQuery(id+"F0.imprint","INTERSECT",VERTEX,{"derivedFrom":[subQ1,subQ0]});Q8=makeQuery(id+"F0.imprint","IMPRINT",FACE,{"disambiguationData":[TD([[makeQuery(id+"F0.imprint","IMPRINT",EDGE,{"disambiguationData":[TD([[subQ2,-1.0]])],"derivedFrom":subQ1}),1.0]])]});}
            var Q9;
            {var subQ0=sQuery(id+"F0.wireOp",EDGE,"E61");var subQ1=sQuery(id+"F0.wireOp",EDGE,"E41");var subQ2=makeQuery(id+"F0.imprint","INTERSECT",VERTEX,{"derivedFrom":[subQ1,subQ0]});Q9=makeQuery(id+"F0.imprint","IMPRINT",FACE,{"disambiguationData":[TD([[makeQuery(id+"F0.imprint","IMPRINT",EDGE,{"disambiguationData":[TD([[subQ2,1.0]])],"derivedFrom":subQ1}),1.0]])]});}
            var Q10;
            {var subQ0=sQuery(id+"F0.wireOp",EDGE,"E41");var subQ1=sQuery(id+"F0.wireOp",EDGE,"E39");var subQ2=makeQuery(id+"F0.imprint","INTERSECT",VERTEX,{"derivedFrom":[subQ1,subQ0]});Q10=makeQuery(id+"F0.imprint","IMPRINT",FACE,{"disambiguationData":[TD([[makeQuery(id+"F0.imprint","IMPRINT",EDGE,{"disambiguationData":[TD([[subQ2,-1.0]])],"derivedFrom":subQ1}),-1.0]])]});}
            var Q11;
            {var subQ0=sQuery(id+"F0.wireOp",EDGE,"E41");var subQ1=sQuery(id+"F0.wireOp",EDGE,"E39");var subQ2=makeQuery(id+"F0.imprint","INTERSECT",VERTEX,{"derivedFrom":[subQ1,subQ0]});Q11=makeQuery(id+"F0.imprint","IMPRINT",FACE,{"disambiguationData":[TD([[makeQuery(id+"F0.imprint","IMPRINT",EDGE,{"disambiguationData":[TD([[subQ2,-1.0]])],"derivedFrom":subQ1}),1.0]])]});}
            var Q12;
            {var subQ0=sQuery(id+"F0.wireOp",EDGE,"E57");var subQ1=sQuery(id+"F0.wireOp",EDGE,"E45");var subQ2=makeQuery(id+"F0.imprint","INTERSECT",VERTEX,{"disambiguationData":[OD(0.0)],"derivedFrom":[subQ1,subQ0]});Q12=makeQuery(id+"F0.imprint","IMPRINT",FACE,{"disambiguationData":[TD([[makeQuery(id+"F0.imprint","IMPRINT",EDGE,{"disambiguationData":[TD([[subQ2,1.0]])],"derivedFrom":subQ1}),1.0]])]});}
            var Q13;
            {var subQ0=sQuery(id+"F0.wireOp",EDGE,"E45");var subQ1=sQuery(id+"F0.wireOp",EDGE,"E43");var subQ2=makeQuery(id+"F0.imprint","INTERSECT",VERTEX,{"derivedFrom":[subQ1,subQ0]});Q13=makeQuery(id+"F0.imprint","IMPRINT",FACE,{"disambiguationData":[TD([[makeQuery(id+"F0.imprint","IMPRINT",EDGE,{"disambiguationData":[TD([[subQ2,-1.0]])],"derivedFrom":subQ1}),1.0]])]});}
            var Q14;
            {var subQ0=sQuery(id+"F0.wireOp",EDGE,"E45");var subQ1=sQuery(id+"F0.wireOp",EDGE,"E43");var subQ2=makeQuery(id+"F0.imprint","INTERSECT",VERTEX,{"derivedFrom":[subQ1,subQ0]});Q14=makeQuery(id+"F0.imprint","IMPRINT",FACE,{"disambiguationData":[TD([[makeQuery(id+"F0.imprint","IMPRINT",EDGE,{"disambiguationData":[TD([[subQ2,-1.0]])],"derivedFrom":subQ1}),-1.0]])]});}
            var Q15;
            {var subQ0=sQuery(id+"F0.wireOp",EDGE,"E50");var subQ1=sQuery(id+"F0.wireOp",EDGE,"E48");var subQ2=makeQuery(id+"F0.imprint","INTERSECT",VERTEX,{"derivedFrom":[subQ1,subQ0]});Q15=makeQuery(id+"F0.imprint","IMPRINT",FACE,{"disambiguationData":[TD([[makeQuery(id+"F0.imprint","IMPRINT",EDGE,{"disambiguationData":[TD([[subQ2,1.0]])],"derivedFrom":subQ1}),1.0]])]});}
            var Q16;
            {var subQ0=sQuery(id+"F0.wireOp",EDGE,"E50");var subQ1=sQuery(id+"F0.wireOp",EDGE,"E48");var subQ2=makeQuery(id+"F0.imprint","INTERSECT",VERTEX,{"derivedFrom":[subQ1,subQ0]});Q16=makeQuery(id+"F0.imprint","IMPRINT",FACE,{"disambiguationData":[TD([[makeQuery(id+"F0.imprint","IMPRINT",EDGE,{"disambiguationData":[TD([[subQ2,-1.0]])],"derivedFrom":subQ1}),1.0]])]});}
            var Q17;
            {var subQ0=sQuery(id+"F0.wireOp",EDGE,"E52");var subQ1=sQuery(id+"F0.wireOp",EDGE,"E48");var subQ2=makeQuery(id+"F0.imprint","INTERSECT",VERTEX,{"disambiguationData":[OD(0.0)],"derivedFrom":[subQ1,subQ0]});Q17=makeQuery(id+"F0.imprint","IMPRINT",FACE,{"disambiguationData":[TD([[makeQuery(id+"F0.imprint","IMPRINT",EDGE,{"disambiguationData":[TD([[subQ2,1.0]])],"derivedFrom":subQ1}),1.0]])]});}
            var Q18;
            {var subQ0=sQuery(id+"F0.wireOp",EDGE,"z3bIMlkc-Sqp3-YFfb-OgYx-sXrnVvqoU3hI");var subQ1=sQuery(id+"F0.wireOp",EDGE,"E37");var subQ2=makeQuery(id+"F0.imprint","INTERSECT",VERTEX,{"disambiguationData":[OD(0.0)],"derivedFrom":[subQ1,subQ0]});Q18=makeQuery(id+"F0.imprint","IMPRINT",FACE,{"disambiguationData":[TD([[makeQuery(id+"F0.imprint","IMPRINT",EDGE,{"disambiguationData":[TD([[subQ2,1.0]])],"derivedFrom":subQ1}),-1.0]])]});}
            var Q19;
            {var subQ0=sQuery(id+"F0.wireOp",EDGE,"LRviyeeh-whrB-Z0BO-Fju1-Ncg8r83Abxvk");var subQ1=sQuery(id+"F0.wireOp",EDGE,"E37");var subQ2=makeQuery(id+"F0.imprint","INTERSECT",VERTEX,{"disambiguationData":[OD(0.0)],"derivedFrom":[subQ1,subQ0]});Q19=makeQuery(id+"F0.imprint","IMPRINT",FACE,{"disambiguationData":[TD([[makeQuery(id+"F0.imprint","IMPRINT",EDGE,{"disambiguationData":[TD([[subQ2,1.0]])],"derivedFrom":subQ1}),-1.0]])]});}
            var Q20;
            {var subQ0=sQuery(id+"F0.wireOp",EDGE,"LRviyeeh-whrB-Z0BO-Fju1-Ncg8r83Abxvk");var subQ1=sQuery(id+"F0.wireOp",EDGE,"E37");var subQ2=makeQuery(id+"F0.imprint","INTERSECT",VERTEX,{"disambiguationData":[OD(1.0)],"derivedFrom":[subQ1,subQ0]});Q20=makeQuery(id+"F0.imprint","IMPRINT",FACE,{"disambiguationData":[TD([[makeQuery(id+"F0.imprint","IMPRINT",EDGE,{"disambiguationData":[TD([[subQ2,-1.0]])],"derivedFrom":subQ1}),-1.0]])]});}
            extrude(context, id + "F3", {"entities" : qUnion([Q0, Q1, Q2, Q3, Q4, Q5, Q6, Q7, Q8, Q9, Q10, Q11, Q12, Q13, Q14, Q15, Q16, Q17, Q18, Q19, Q20]), "depth" : 9 * mm, "offsetDistance" : 25 * mm});
        }
        {
            var Q0;
            {var subQ0=sQuery(id+"F0.wireOp",EDGE,"E57");var subQ1=sQuery(id+"F0.wireOp",EDGE,"E43");var subQ2=makeQuery(id+"F0.imprint","INTERSECT",VERTEX,{"derivedFrom":[subQ1,subQ0]});Q0=makeQuery(id+"F0.imprint","IMPRINT",FACE,{"disambiguationData":[TD([[makeQuery(id+"F0.imprint","IMPRINT",EDGE,{"disambiguationData":[TD([[subQ2,1.0]])],"derivedFrom":subQ1}),1.0]])]});}
            var Q1;
            {var subQ0=sQuery(id+"F0.wireOp",EDGE,"E57");var subQ1=sQuery(id+"F0.wireOp",EDGE,"E43");var subQ2=makeQuery(id+"F0.imprint","INTERSECT",VERTEX,{"derivedFrom":[subQ1,subQ0]});Q1=makeQuery(id+"F0.imprint","IMPRINT",FACE,{"disambiguationData":[TD([[makeQuery(id+"F0.imprint","IMPRINT",EDGE,{"disambiguationData":[TD([[subQ2,1.0]])],"derivedFrom":subQ1}),-1.0]])]});}
            var Q2;
            {var subQ0=sQuery(id+"F0.wireOp",EDGE,"E57");var subQ1=sQuery(id+"F0.wireOp",EDGE,"E46");var subQ2=makeQuery(id+"F0.imprint","INTERSECT",VERTEX,{"disambiguationData":[OD(0.0)],"derivedFrom":[subQ1,subQ0]});Q2=makeQuery(id+"F0.imprint","IMPRINT",FACE,{"disambiguationData":[TD([[makeQuery(id+"F0.imprint","IMPRINT",EDGE,{"disambiguationData":[TD([[subQ2,1.0]])],"derivedFrom":subQ1}),1.0]])]});}
            var Q3;
            {var subQ0=sQuery(id+"F0.wireOp",EDGE,"E61");var subQ1=sQuery(id+"F0.wireOp",EDGE,"E42");var subQ2=makeQuery(id+"F0.imprint","INTERSECT",VERTEX,{"derivedFrom":[subQ1,subQ0]});Q3=makeQuery(id+"F0.imprint","IMPRINT",FACE,{"disambiguationData":[TD([[makeQuery(id+"F0.imprint","IMPRINT",EDGE,{"disambiguationData":[TD([[subQ2,1.0]])],"derivedFrom":subQ1}),1.0]])]});}
            var Q4;
            {var subQ1=sQuery(id+"F0.wireOp",EDGE,"E39");var subQ3=sQuery(id+"F0.wireOp",EDGE,"E42");var subQ4=makeQuery(id+"F0.imprint","INTERSECT",VERTEX,{"derivedFrom":[subQ1,subQ3]});Q4=makeQuery(id+"F0.imprint","IMPRINT",FACE,{"disambiguationData":[TD([[makeQuery(id+"F0.imprint","IMPRINT",EDGE,{"disambiguationData":[TD([[subQ4,-1.0]])],"derivedFrom":subQ3}),1.0]])]});}
            var Q5;
            {var subQ1=sQuery(id+"F0.wireOp",EDGE,"E39");var subQ3=sQuery(id+"F0.wireOp",EDGE,"E42");var subQ4=makeQuery(id+"F0.imprint","INTERSECT",VERTEX,{"derivedFrom":[subQ1,subQ3]});Q5=makeQuery(id+"F0.imprint","IMPRINT",FACE,{"disambiguationData":[TD([[makeQuery(id+"F0.imprint","IMPRINT",EDGE,{"disambiguationData":[TD([[subQ4,1.0]])],"derivedFrom":subQ3}),1.0]])]});}
            var Q6;
            {var subQ0=sQuery(id+"F0.wireOp",EDGE,"z3bIMlkc-Sqp3-YFfb-OgYx-sXrnVvqoU3hI");var subQ1=sQuery(id+"F0.wireOp",EDGE,"E36");var subQ2=makeQuery(id+"F0.imprint","INTERSECT",VERTEX,{"derivedFrom":[subQ1,subQ0]});Q6=makeQuery(id+"F0.imprint","IMPRINT",FACE,{"disambiguationData":[TD([[makeQuery(id+"F0.imprint","IMPRINT",EDGE,{"disambiguationData":[TD([[subQ2,1.0]])],"derivedFrom":subQ1}),-1.0]])]});}
            var Q7;
            {var subQ0=sQuery(id+"F0.wireOp",EDGE,"z3bIMlkc-Sqp3-YFfb-OgYx-sXrnVvqoU3hI");var subQ1=sQuery(id+"F0.wireOp",EDGE,"E36");var subQ2=makeQuery(id+"F0.imprint","INTERSECT",VERTEX,{"derivedFrom":[subQ1,subQ0]});Q7=makeQuery(id+"F0.imprint","IMPRINT",FACE,{"disambiguationData":[TD([[makeQuery(id+"F0.imprint","IMPRINT",EDGE,{"disambiguationData":[TD([[subQ2,1.0]])],"derivedFrom":subQ1}),1.0]])]});}
            var Q8;
            {var subQ0=sQuery(id+"F0.wireOp",EDGE,"z3bIMlkc-Sqp3-YFfb-OgYx-sXrnVvqoU3hI");var subQ1=sQuery(id+"F0.wireOp",EDGE,"E37");var subQ2=makeQuery(id+"F0.imprint","INTERSECT",VERTEX,{"disambiguationData":[OD(0.0)],"derivedFrom":[subQ1,subQ0]});Q8=makeQuery(id+"F0.imprint","IMPRINT",FACE,{"disambiguationData":[TD([[makeQuery(id+"F0.imprint","IMPRINT",EDGE,{"disambiguationData":[TD([[subQ2,-1.0]])],"derivedFrom":subQ1}),1.0]])]});}
            var Q9;
            {var subQ1=sQuery(id+"F0.wireOp",EDGE,"9S27bfH2-aeVg-8c6K-cwQt-1v0k5dwx2PAc");var subQ3=sQuery(id+"F0.wireOp",EDGE,"Suqf36BG-M7e0-ZgLu-wpgL-xeVtndynmz1x");var subQ4=makeQuery(id+"F0.imprint","INTERSECT",VERTEX,{"derivedFrom":[subQ1,subQ3]});Q9=makeQuery(id+"F0.imprint","IMPRINT",FACE,{"disambiguationData":[TD([[makeQuery(id+"F0.imprint","IMPRINT",EDGE,{"disambiguationData":[TD([[subQ4,1.0]])],"derivedFrom":subQ3}),1.0]])]});}
            var Q10;
            {var subQ1=sQuery(id+"F0.wireOp",EDGE,"Gpz7nxuA-fGOU-zDca-uDqp-oelFocvOXtPt");var subQ3=sQuery(id+"F0.wireOp",EDGE,"Suqf36BG-M7e0-ZgLu-wpgL-xeVtndynmz1x");var subQ4=makeQuery(id+"F0.imprint","INTERSECT",VERTEX,{"derivedFrom":[subQ1,subQ3]});Q10=makeQuery(id+"F0.imprint","IMPRINT",FACE,{"disambiguationData":[TD([[makeQuery(id+"F0.imprint","IMPRINT",EDGE,{"disambiguationData":[TD([[subQ4,-1.0]])],"derivedFrom":subQ3}),1.0]])]});}
            var Q11;
            {var subQ1=sQuery(id+"F0.wireOp",EDGE,"9S27bfH2-aeVg-8c6K-cwQt-1v0k5dwx2PAc");var subQ3=sQuery(id+"F0.wireOp",EDGE,"Suqf36BG-M7e0-ZgLu-wpgL-xeVtndynmz1x");var subQ4=makeQuery(id+"F0.imprint","INTERSECT",VERTEX,{"derivedFrom":[subQ1,subQ3]});Q11=makeQuery(id+"F0.imprint","IMPRINT",FACE,{"disambiguationData":[TD([[makeQuery(id+"F0.imprint","IMPRINT",EDGE,{"disambiguationData":[TD([[subQ4,-1.0]])],"derivedFrom":subQ3}),1.0]])]});}
            var Q12;
            {var subQ0=sQuery(id+"F0.wireOp",EDGE,"WzKnqnnp-cW6H-dtaq-a9nc-BIZvJngSIy6v");var subQ1=sQuery(id+"F0.wireOp",EDGE,"Suqf36BG-M7e0-ZgLu-wpgL-xeVtndynmz1x");var subQ2=makeQuery(id+"F0.imprint","INTERSECT",VERTEX,{"derivedFrom":[subQ1,subQ0]});Q12=makeQuery(id+"F0.imprint","IMPRINT",FACE,{"disambiguationData":[TD([[makeQuery(id+"F0.imprint","IMPRINT",EDGE,{"disambiguationData":[TD([[subQ2,-1.0]])],"derivedFrom":subQ1}),1.0]])]});}
            var Q13;
            {var subQ1=sQuery(id+"F0.wireOp",EDGE,"Gpz7nxuA-fGOU-zDca-uDqp-oelFocvOXtPt");var subQ3=sQuery(id+"F0.wireOp",EDGE,"Suqf36BG-M7e0-ZgLu-wpgL-xeVtndynmz1x");var subQ4=makeQuery(id+"F0.imprint","INTERSECT",VERTEX,{"derivedFrom":[subQ1,subQ3]});Q13=makeQuery(id+"F0.imprint","IMPRINT",FACE,{"disambiguationData":[TD([[makeQuery(id+"F0.imprint","IMPRINT",EDGE,{"disambiguationData":[TD([[subQ4,1.0]])],"derivedFrom":subQ3}),1.0]])]});}
            var Q14;
            {var subQ0=sQuery(id+"F0.wireOp",EDGE,"E52");var subQ1=sQuery(id+"F0.wireOp",EDGE,"E49");var subQ2=makeQuery(id+"F0.imprint","INTERSECT",VERTEX,{"disambiguationData":[OD(0.0)],"derivedFrom":[subQ1,subQ0]});Q14=makeQuery(id+"F0.imprint","IMPRINT",FACE,{"disambiguationData":[TD([[makeQuery(id+"F0.imprint","IMPRINT",EDGE,{"disambiguationData":[TD([[subQ2,1.0]])],"derivedFrom":subQ1}),1.0]])]});}
            var Q15;
            {var subQ0=sQuery(id+"F0.wireOp",EDGE,"E50");var subQ1=sQuery(id+"F0.wireOp",EDGE,"E49");var subQ2=makeQuery(id+"F0.imprint","INTERSECT",VERTEX,{"derivedFrom":[subQ1,subQ0]});Q15=makeQuery(id+"F0.imprint","IMPRINT",FACE,{"disambiguationData":[TD([[makeQuery(id+"F0.imprint","IMPRINT",EDGE,{"disambiguationData":[TD([[subQ2,-1.0]])],"derivedFrom":subQ1}),1.0]])]});}
            var Q16;
            {var subQ0=sQuery(id+"F0.wireOp",EDGE,"E50");var subQ1=sQuery(id+"F0.wireOp",EDGE,"E49");var subQ2=makeQuery(id+"F0.imprint","INTERSECT",VERTEX,{"derivedFrom":[subQ1,subQ0]});Q16=makeQuery(id+"F0.imprint","IMPRINT",FACE,{"disambiguationData":[TD([[makeQuery(id+"F0.imprint","IMPRINT",EDGE,{"disambiguationData":[TD([[subQ2,1.0]])],"derivedFrom":subQ1}),1.0]])]});}
            var Q17;
            Q17=makeQuery(id+"F0.imprint","IMPRINT",FACE,{"disambiguationData":[TD([[makeQuery(id+"F0.imprint","IMPRINT",EDGE,{"derivedFrom":sQuery(id+"F0.wireOp",EDGE,"E26")}),-1.0]])]});
            var Q18;
            {var subQ0=sQuery(id+"F0.wireOp",EDGE,"LRviyeeh-whrB-Z0BO-Fju1-Ncg8r83Abxvk");var subQ1=sQuery(id+"F0.wireOp",EDGE,"E37");var subQ2=makeQuery(id+"F0.imprint","INTERSECT",VERTEX,{"disambiguationData":[OD(0.0)],"derivedFrom":[subQ1,subQ0]});Q18=makeQuery(id+"F0.imprint","IMPRINT",FACE,{"disambiguationData":[TD([[makeQuery(id+"F0.imprint","IMPRINT",EDGE,{"disambiguationData":[TD([[subQ2,1.0]])],"derivedFrom":subQ1}),1.0]])]});}
            var Q19;
            {var subQ0=sQuery(id+"F0.wireOp",EDGE,"LRviyeeh-whrB-Z0BO-Fju1-Ncg8r83Abxvk");var subQ1=sQuery(id+"F0.wireOp",EDGE,"E37");var subQ2=makeQuery(id+"F0.imprint","INTERSECT",VERTEX,{"disambiguationData":[OD(1.0)],"derivedFrom":[subQ1,subQ0]});Q19=makeQuery(id+"F0.imprint","IMPRINT",FACE,{"disambiguationData":[TD([[makeQuery(id+"F0.imprint","IMPRINT",EDGE,{"disambiguationData":[TD([[subQ2,-1.0]])],"derivedFrom":subQ1}),1.0]])]});}
            var Q20;
            {var subQ0=sQuery(id+"F0.wireOp",EDGE,"z3bIMlkc-Sqp3-YFfb-OgYx-sXrnVvqoU3hI");var subQ1=sQuery(id+"F0.wireOp",EDGE,"E37");var subQ2=makeQuery(id+"F0.imprint","INTERSECT",VERTEX,{"disambiguationData":[OD(0.0)],"derivedFrom":[subQ1,subQ0]});Q20=makeQuery(id+"F0.imprint","IMPRINT",FACE,{"disambiguationData":[TD([[makeQuery(id+"F0.imprint","IMPRINT",EDGE,{"disambiguationData":[TD([[subQ2,1.0]])],"derivedFrom":subQ1}),1.0]])]});}
            var Q21;
            Q21=makeQuery(id+"F0.imprint","IMPRINT",FACE,{"disambiguationData":[TD([[makeQuery(id+"F0.imprint","IMPRINT",EDGE,{"derivedFrom":sQuery(id+"F0.wireOp",EDGE,"E26")}),1.0]])]});
            extrude(context, id + "F4", {"entities" : qUnion([Q0, Q1, Q2, Q3, Q4, Q5, Q6, Q7, Q8, Q9, Q10, Q11, Q12, Q13, Q14, Q15, Q16, Q17, Q18, Q19, Q20, Q21]), "depth" : 3 * mm, "offsetDistance" : 25 * mm});
        }
    });
